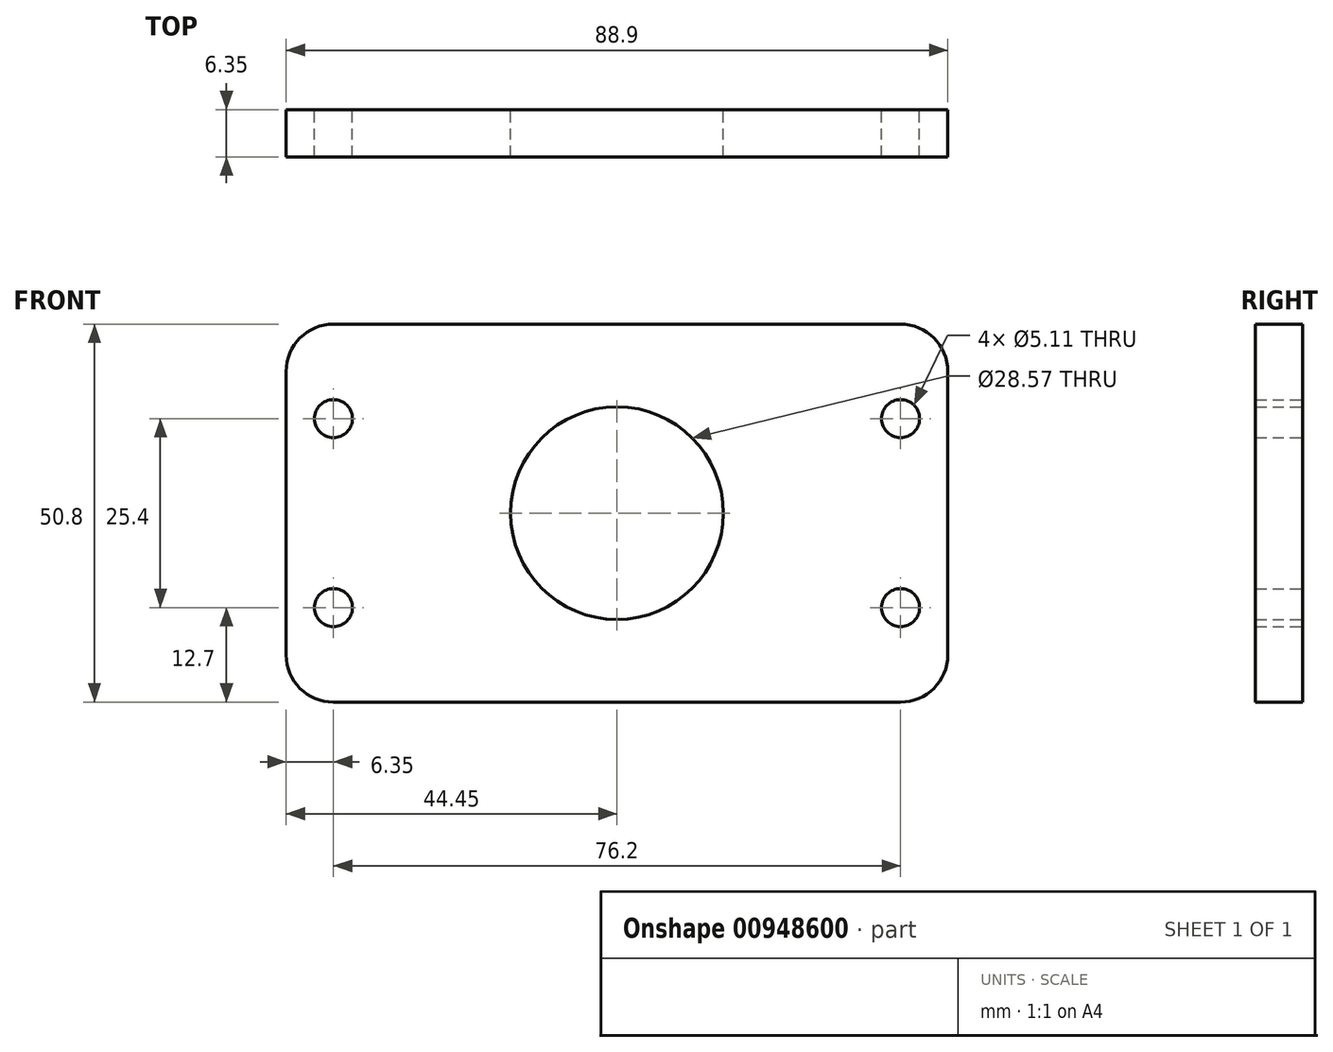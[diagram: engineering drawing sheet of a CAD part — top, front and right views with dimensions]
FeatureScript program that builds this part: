
annotation { "Feature Type Name" : "Feature", "Feature Type Description" : "" }
export const myFeature = defineFeature(function(context is Context, id is Id, definition is map)
    precondition{}
    {
        {
            var Q0;
            Q0=qCreatedBy(makeId("Front.planeOp"),FACE);
            var sketch = newSketch(context, id + "F0", { "sketchPlane" : qUnion([Q0])});
            skLineSegment(sketch, "E0.bottom", {"start": v(-44.45, 25.4) * mm, "end": v(44.45, 25.4) * mm});
            skLineSegment(sketch, "E0.top", {"start": v(-44.45, -25.4) * mm, "end": v(44.45, -25.4) * mm});
            skLineSegment(sketch, "E0.left", {"start": v(-44.45, 25.4) * mm, "end": v(-44.45, -25.4) * mm});
            skLineSegment(sketch, "E0.right", {"start": v(44.45, 25.4) * mm, "end": v(44.45, -25.4) * mm});
            skPoint(sketch, "E0.middle", {"position": v(0, 0) * mm});
            skCircle(sketch, "E1", {"center": v(0, 0) * mm, "radius": 14.29 * mm});
            skLineSegment(sketch, "E2.bottom", {"start": v(-38.1, 12.7) * mm, "end": v(38.1, 12.7) * mm, "construction": true});
            skLineSegment(sketch, "E2.top", {"start": v(-38.1, -12.7) * mm, "end": v(38.1, -12.7) * mm, "construction": true});
            skLineSegment(sketch, "E2.left", {"start": v(-38.1, 12.7) * mm, "end": v(-38.1, -12.7) * mm, "construction": true});
            skLineSegment(sketch, "E2.right", {"start": v(38.1, 12.7) * mm, "end": v(38.1, -12.7) * mm, "construction": true});
            skCircle(sketch, "E3", {"center": v(-38.1, -12.7) * mm, "radius": 2.55 * mm});
            skCircle(sketch, "E4", {"center": v(-38.1, 12.7) * mm, "radius": 2.55 * mm});
            skCircle(sketch, "E5", {"center": v(38.1, 12.7) * mm, "radius": 2.55 * mm});
            skCircle(sketch, "E6", {"center": v(38.1, -12.7) * mm, "radius": 2.55 * mm});
            skSolve(sketch);
        }
        {
            var Q0;
            Q0=makeQuery(id+"F0.imprint","IMPRINT",FACE,{"disambiguationData":[TD([[makeQuery(id+"F0.imprint","IMPRINT",EDGE,{"derivedFrom":sQuery(id+"F0.wireOp",EDGE,"E0.bottom")}),-1.0]])]});
            extrude(context, id + "F1", {"entities" : qUnion([Q0]), "depth" : 6.35 * mm, "offsetDistance" : 25.4 * mm});
        }
        {
            var Q0;
            Q0=makeQuery(id+"F1.opExtrude","SWEPT_EDGE",EDGE,{"disambiguationData":[OSD([sQuery(id+"F0.wireOp",EDGE,"E0.bottom"),sQuery(id+"F0.wireOp",EDGE,"E0.left")])]});
            var Q1;
            Q1=makeQuery(id+"F1.opExtrude","SWEPT_EDGE",EDGE,{"disambiguationData":[OSD([sQuery(id+"F0.wireOp",EDGE,"E0.top"),sQuery(id+"F0.wireOp",EDGE,"E0.left")])]});
            var Q2;
            Q2=makeQuery(id+"F1.opExtrude","SWEPT_EDGE",EDGE,{"disambiguationData":[OSD([sQuery(id+"F0.wireOp",EDGE,"E0.top"),sQuery(id+"F0.wireOp",EDGE,"E0.right")])]});
            var Q3;
            Q3=makeQuery(id+"F1.opExtrude","SWEPT_EDGE",EDGE,{"disambiguationData":[OSD([sQuery(id+"F0.wireOp",EDGE,"E0.bottom"),sQuery(id+"F0.wireOp",EDGE,"E0.right")])]});
            fillet(context, id + "F2", {"entities" : qUnion([Q0, Q1, Q2, Q3]), "radius" : 6.35 * mm, "tangentPropagation" : true, "allowEdgeOverflow" : false});
        }
    });
